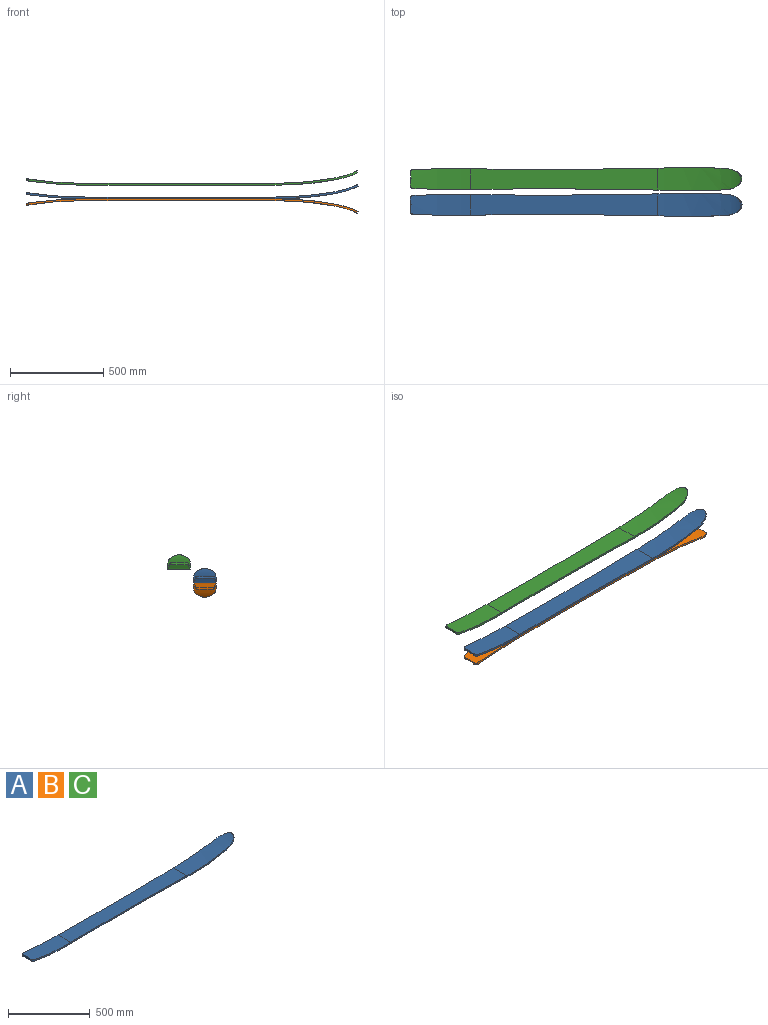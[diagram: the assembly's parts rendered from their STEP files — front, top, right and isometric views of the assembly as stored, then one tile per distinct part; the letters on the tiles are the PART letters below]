
ASSEMBLY  parts=3 mates=1
PART A: 22 faces, bbox 1775.7x122x76.7 mm
  f0: bspline ~63.28x10.44mm, area 637.7mm2, adj f1,f15,f16,f19
  f1: bspline ~18.13x15.65mm, area 258.7mm2, adj f0,f2,f16,f19
  f2: bspline ~256.73x31.07mm, area 2570.1mm2, adj f1,f3,f16,f19
  f3: bspline ~55.13x10.59mm, area 550.3mm2, adj f2,f4,f16,f19
  f4: cylinder r=27850.68mm len=1000mm, axis (0,0,1), area 10000.6mm2, adj f3,f5,f17,f20
  f5: bspline ~34.66x10.27mm, area 345.9mm2, adj f4,f6,f18,f21
  f6: bspline ~293.93x37.87mm, area 2946mm2, adj f5,f7,f18,f21
  f7: bspline ~37.95x17.88mm, area 366.9mm2, adj f6,f8,f18,f21
  f8: bspline ~113.79x88.09mm, area 2302.3mm2, adj f7,f9,f18,f21
  f9: bspline ~37.95x17.88mm, area 366.9mm2, adj f8,f10,f18,f21
  f10: bspline ~293.93x37.87mm, area 2946mm2, adj f9,f11,f18,f21
  f11: bspline ~34.66x10.27mm, area 345.9mm2, adj f10,f12,f18,f21
  f12: cylinder r=27850.68mm len=1000mm, axis (0,0,1), area 10000.6mm2, adj f11,f13,f17,f20
  f13: bspline ~55.13x10.59mm, area 550.3mm2, adj f12,f14,f16,f19
  f14: bspline ~256.73x31.07mm, area 2570.1mm2, adj f13,f15,f16,f19
  f15: bspline ~18.13x15.65mm, area 258.7mm2, adj f0,f14,f16,f19
  f16: extruded ~323.89x112mm, area 35197.2mm2, adj f0,f1,f2,f3,f13,f14,f15,f17
  f17: plane 1000x117.35mm, normal (0,0,1), area 107424.1mm2, adj f4,f12,f16,f18
  f18: extruded ~445.01x122mm, area 51420.7mm2, adj f5,f6,f7,f8,f9,f10,f11,f17
  f19: extruded ~325.66x112mm, area 35242mm2, adj f0,f1,f2,f3,f13,f14,f15,f20
  f20: plane 1000x117.35mm, normal (0,0,-1), area 107424.1mm2, adj f4,f12,f19,f21
  f21: extruded ~450.01x122mm, area 51876.4mm2, adj f5,f6,f7,f8,f9,f10,f11,f20
PART B: same geometry as A
PART C: same geometry as A
PLACE A t=(-195.65,-385.39,164.84)mm
PLACE B rot(axis=(1,0,0),180deg) t=(-195.65,-385.39,-15.16)mm
PLACE C t=(-195.68,-247.6,238.45)mm
MATE fastened B.f20 <-> A.f20  axis (0,0,1) through (-859.54,-385.39,74.84)mm
